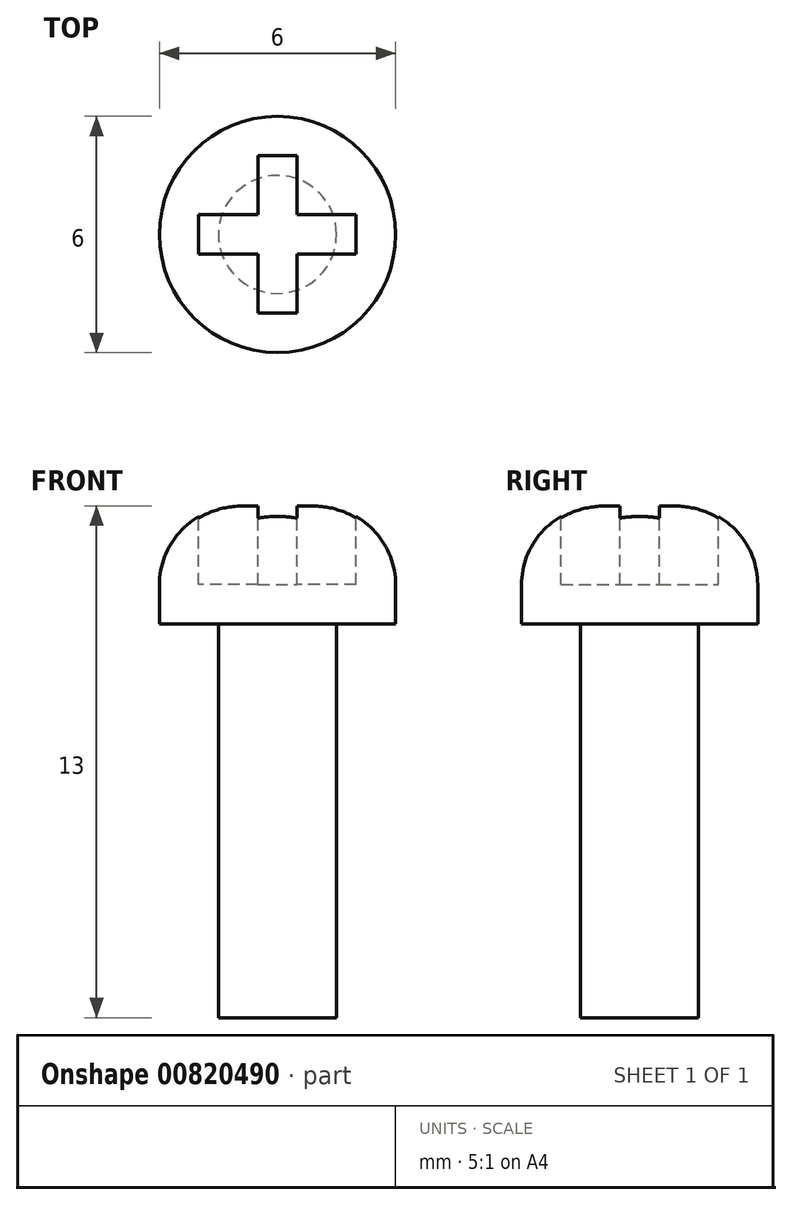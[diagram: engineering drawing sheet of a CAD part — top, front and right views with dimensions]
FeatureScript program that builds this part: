
annotation { "Feature Type Name" : "Feature", "Feature Type Description" : "" }
export const myFeature = defineFeature(function(context is Context, id is Id, definition is map)
    precondition{}
    {
        {
            var Q0;
            Q0=qCreatedBy(makeId("Top.planeOp"),FACE);
            var sketch = newSketch(context, id + "F0", { "sketchPlane" : qUnion([Q0])});
            skCircle(sketch, "E0", {"center": v(0, 0) * mm, "radius": 1.5 * mm});
            skSolve(sketch);
        }
        {
            var Q0;
            Q0 = qSketchRegion(id + "F0", true);
            extrude(context, id + "F1", {"entities" : qUnion([Q0]), "oppositeDirection" : true, "depth" : 10 * mm, "offsetDistance" : 25 * mm});
        }
        {
            var Q0;
            Q0=makeQuery(id+"F1.opExtrude","CAP_FACE",FACE,{"disambiguationData":[OSD([sQuery(id+"F0.wireOp",EDGE,"E0")])],"isStart":true});
            var sketch = newSketch(context, id + "F2", { "sketchPlane" : qUnion([Q0])});
            skCircle(sketch, "E1", {"center": v(0, 0) * mm, "radius": 3 * mm});
            skSolve(sketch);
        }
        {
            var Q0;
            Q0=makeQuery(id+"F2.imprint","IMPRINT",FACE,{"disambiguationData":[TD([[makeQuery(id+"F2.imprint","IMPRINT",EDGE,{"derivedFrom":sQuery(id+"F2.wireOp",EDGE,"E1")}),1.0]])]});
            var Q1;
            Q1=makeQuery(id+"F2.imprint","IMPRINT",FACE,{"disambiguationData":[TD([[makeQuery(id+"F2.imprint","IMPRINT",EDGE,{"derivedFrom":makeQuery(id+"F1.opExtrude","CAP_EDGE",EDGE,{"disambiguationData":[OSD([sQuery(id+"F0.wireOp",EDGE,"E0")])],"isStart":true})}),1.0]])]});
            extrude(context, id + "F3", {"entities" : qUnion([Q0, Q1]), "operationType" : NewBodyOperationType.ADD, "depth" : 3 * mm, "offsetDistance" : 25 * mm});
        }
        {
            var Q0;
            Q0=makeQuery(id+"F3.opExtrude","CAP_FACE",FACE,{"disambiguationData":[OSD([sQuery(id+"F2.wireOp",EDGE,"E1")])],"isStart":false});
            var sketch = newSketch(context, id + "F4", { "sketchPlane" : qUnion([Q0])});
            skLineSegment(sketch, "E2.bottom", {"start": v(2, -0.5) * mm, "end": v(-2, -0.5) * mm});
            skLineSegment(sketch, "E2.top", {"start": v(2, 0.5) * mm, "end": v(-2, 0.5) * mm});
            skLineSegment(sketch, "E2.left", {"start": v(2, -0.5) * mm, "end": v(2, 0.5) * mm});
            skLineSegment(sketch, "E2.right", {"start": v(-2, -0.5) * mm, "end": v(-2, 0.5) * mm});
            skPoint(sketch, "E2.middle", {"position": v(0, 0) * mm});
            skLineSegment(sketch, "E3.bottom", {"start": v(-0.5, -2) * mm, "end": v(0.5, -2) * mm});
            skLineSegment(sketch, "E3.top", {"start": v(-0.5, 2) * mm, "end": v(0.5, 2) * mm});
            skLineSegment(sketch, "E3.left", {"start": v(-0.5, -2) * mm, "end": v(-0.5, 2) * mm});
            skLineSegment(sketch, "E3.right", {"start": v(0.5, -2) * mm, "end": v(0.5, 2) * mm});
            skSolve(sketch);
        }
        {
            var Q0;
            {var subQ0=sQuery(id+"F4.wireOp",EDGE,"E2.right");Q0=makeQuery(id+"F4.imprint","IMPRINT",FACE,{"disambiguationData":[TD([[makeQuery(id+"F4.imprint","IMPRINT",EDGE,{"derivedFrom":subQ0}),-1.0]])]});}
            var Q1;
            {var subQ5=sQuery(id+"F4.wireOp",EDGE,"E3.top");Q1=makeQuery(id+"F4.imprint","IMPRINT",FACE,{"disambiguationData":[TD([[makeQuery(id+"F4.imprint","IMPRINT",EDGE,{"derivedFrom":subQ5}),-1.0]])]});}
            var Q2;
            {var subQ0=sQuery(id+"F4.wireOp",EDGE,"E3.right");var subQ1=sQuery(id+"F4.wireOp",EDGE,"E2.bottom");var subQ2=makeQuery(id+"F4.imprint","INTERSECT",VERTEX,{"derivedFrom":[subQ1,subQ0]});Q2=makeQuery(id+"F4.imprint","IMPRINT",FACE,{"disambiguationData":[TD([[makeQuery(id+"F4.imprint","IMPRINT",EDGE,{"disambiguationData":[TD([[subQ2,-1.0]])],"derivedFrom":subQ1}),-1.0]])]});}
            var Q3;
            {var subQ0=sQuery(id+"F4.wireOp",EDGE,"E2.left");Q3=makeQuery(id+"F4.imprint","IMPRINT",FACE,{"disambiguationData":[TD([[makeQuery(id+"F4.imprint","IMPRINT",EDGE,{"derivedFrom":subQ0}),1.0]])]});}
            var Q4;
            {var subQ5=sQuery(id+"F4.wireOp",EDGE,"E3.bottom");Q4=makeQuery(id+"F4.imprint","IMPRINT",FACE,{"disambiguationData":[TD([[makeQuery(id+"F4.imprint","IMPRINT",EDGE,{"derivedFrom":subQ5}),1.0]])]});}
            extrude(context, id + "F5", {"entities" : qUnion([Q0, Q1, Q2, Q3, Q4]), "operationType" : NewBodyOperationType.REMOVE, "oppositeDirection" : true, "depth" : 2 * mm, "offsetDistance" : 25 * mm});
        }
        {
            var Q0;
            Q0=makeQuery(id+"F3.opExtrude","CAP_EDGE",EDGE,{"disambiguationData":[OSD([sQuery(id+"F2.wireOp",EDGE,"E1")])],"isStart":false});
            fillet(context, id + "F6", {"entities" : qUnion([Q0]), "radius" : 2 * mm, "tangentPropagation" : true, "allowEdgeOverflow" : false});
        }
    });
